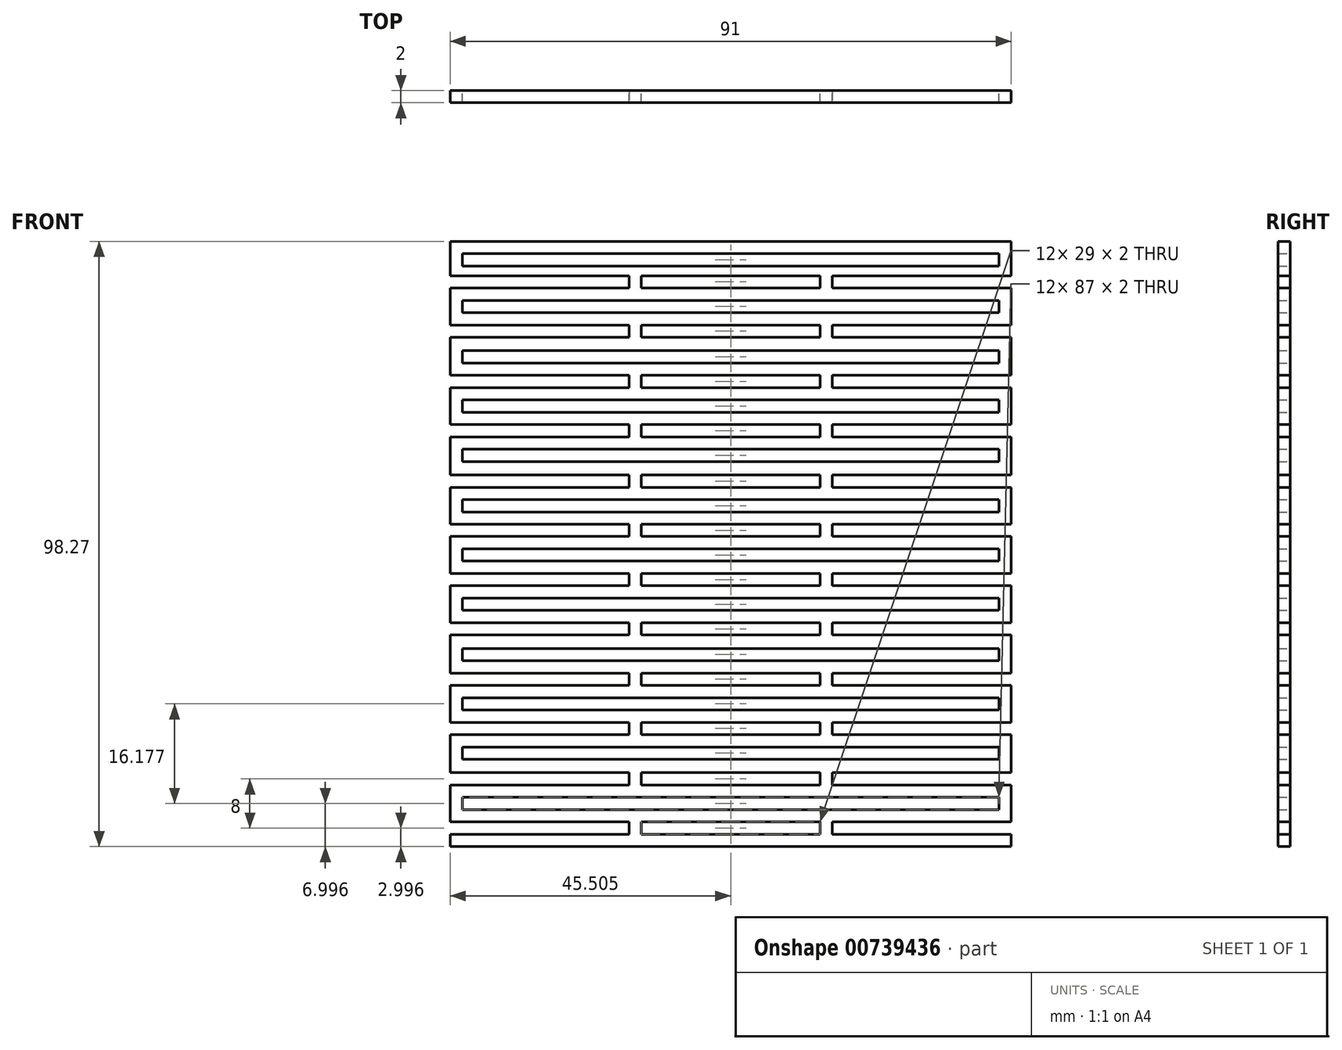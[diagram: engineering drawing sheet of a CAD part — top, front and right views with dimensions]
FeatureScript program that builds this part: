
annotation { "Feature Type Name" : "Feature", "Feature Type Description" : "" }
export const myFeature = defineFeature(function(context is Context, id is Id, definition is map)
    precondition{}
    {
        {
            var Q0;
            Q0=qCreatedBy(makeId("Front.planeOp"),FACE);
            var sketch = newSketch(context, id + "F0", { "sketchPlane" : qUnion([Q0])});
            skLineSegment(sketch, "E0.top", {"start": v(-74.18, -54.88) * mm, "end": v(16.82, -54.88) * mm});
            skLineSegment(sketch, "E0.left", {"start": v(-74.18, 45.12) * mm, "end": v(-74.18, 37.82) * mm});
            skLineSegment(sketch, "E0.right", {"start": v(16.82, 45.12) * mm, "end": v(16.82, 37.82) * mm});
            skLineSegment(sketch, "E1.left", {"start": v(-74.18, -52.88) * mm, "end": v(-74.18, -53.7) * mm});
            skLineSegment(sketch, "E2.bottom", {"start": v(-74.18, -50.88) * mm, "end": v(-45.18, -50.88) * mm});
            skLineSegment(sketch, "E2.top", {"start": v(-74.18, -52.88) * mm, "end": v(-45.18, -52.88) * mm});
            skLineSegment(sketch, "E2.right", {"start": v(-45.18, -50.88) * mm, "end": v(-45.18, -52.88) * mm});
            skLineSegment(sketch, "E3.bottom", {"start": v(16.82, -50.88) * mm, "end": v(-12.18, -50.88) * mm});
            skLineSegment(sketch, "E3.top", {"start": v(16.82, -52.88) * mm, "end": v(-12.18, -52.88) * mm});
            skLineSegment(sketch, "E3.right", {"start": v(-12.18, -50.88) * mm, "end": v(-12.18, -52.88) * mm});
            skPoint(sketch, "E4.oppositeSnap0", {"position": v(2.32, -52.88) * mm});
            skLineSegment(sketch, "E4.bottom", {"start": v(-43.18, -50.88) * mm, "end": v(-14.18, -50.88) * mm});
            skLineSegment(sketch, "E4.top", {"start": v(-43.18, -52.88) * mm, "end": v(-14.18, -52.88) * mm});
            skLineSegment(sketch, "E4.left", {"start": v(-43.18, -50.88) * mm, "end": v(-43.18, -52.88) * mm});
            skLineSegment(sketch, "E4.right", {"start": v(-14.18, -50.88) * mm, "end": v(-14.18, -52.88) * mm});
            skLineSegment(sketch, "E5.bottom", {"start": v(-72.18, -46.88) * mm, "end": v(14.82, -46.88) * mm});
            skLineSegment(sketch, "E5.top", {"start": v(-72.18, -48.88) * mm, "end": v(14.82, -48.88) * mm});
            skLineSegment(sketch, "E5.left", {"start": v(-72.18, -46.88) * mm, "end": v(-72.18, -48.88) * mm});
            skLineSegment(sketch, "E5.right", {"start": v(14.82, -46.88) * mm, "end": v(14.82, -48.88) * mm});
            skLineSegment(sketch, "E6.MirrorCS", {"start": v(-72.18, -40.7) * mm, "end": v(14.82, -40.7) * mm});
            skLineSegment(sketch, "E7.MirrorCS", {"start": v(-72.18, -38.7) * mm, "end": v(14.82, -38.7) * mm});
            skLineSegment(sketch, "E8.MirrorCS", {"start": v(14.82, -40.7) * mm, "end": v(14.82, -38.7) * mm});
            skLineSegment(sketch, "E9.MirrorCS", {"start": v(-72.18, -40.7) * mm, "end": v(-72.18, -38.7) * mm});
            skLineSegment(sketch, "E10.MirrorCS", {"start": v(-74.18, -36.7) * mm, "end": v(-45.18, -36.7) * mm});
            skLineSegment(sketch, "E11.MirrorCS", {"start": v(-74.18, -34.7) * mm, "end": v(-45.18, -34.7) * mm});
            skLineSegment(sketch, "E12.MirrorCS", {"start": v(-43.18, -36.7) * mm, "end": v(-43.18, -34.7) * mm});
            skLineSegment(sketch, "E13.MirrorCS", {"start": v(-45.18, -36.7) * mm, "end": v(-45.18, -34.7) * mm});
            skLineSegment(sketch, "E14.MirrorCS", {"start": v(-43.18, -36.7) * mm, "end": v(-14.18, -36.7) * mm});
            skLineSegment(sketch, "E15.MirrorCS", {"start": v(-43.18, -34.7) * mm, "end": v(-14.18, -34.7) * mm});
            skLineSegment(sketch, "E16.MirrorCS", {"start": v(-14.18, -36.7) * mm, "end": v(-14.18, -34.7) * mm});
            skLineSegment(sketch, "E17.MirrorCS", {"start": v(-12.18, -36.7) * mm, "end": v(-12.18, -34.7) * mm});
            skLineSegment(sketch, "E18.MirrorCS", {"start": v(16.82, -36.7) * mm, "end": v(-12.18, -36.7) * mm});
            skLineSegment(sketch, "E19.MirrorCS", {"start": v(16.82, -34.7) * mm, "end": v(-12.18, -34.7) * mm});
            skLineSegment(sketch, "E20.MirrorCS", {"start": v(-74.18, -44.88) * mm, "end": v(-45.18, -44.88) * mm});
            skLineSegment(sketch, "E21.MirrorCS", {"start": v(-74.18, -42.88) * mm, "end": v(-45.18, -42.88) * mm});
            skLineSegment(sketch, "E22.MirrorCS", {"start": v(-43.18, -44.88) * mm, "end": v(-43.18, -42.88) * mm});
            skLineSegment(sketch, "E23.MirrorCS", {"start": v(-45.18, -44.88) * mm, "end": v(-45.18, -42.88) * mm});
            skLineSegment(sketch, "E24.MirrorCS", {"start": v(-43.18, -44.88) * mm, "end": v(-14.18, -44.88) * mm});
            skLineSegment(sketch, "E25.MirrorCS", {"start": v(-43.18, -42.88) * mm, "end": v(-14.18, -42.88) * mm});
            skLineSegment(sketch, "E26.MirrorCS", {"start": v(-14.18, -44.88) * mm, "end": v(-14.18, -42.88) * mm});
            skLineSegment(sketch, "E27.MirrorCS", {"start": v(-12.18, -44.88) * mm, "end": v(-12.18, -42.88) * mm});
            skLineSegment(sketch, "E28.MirrorCS", {"start": v(16.82, -44.88) * mm, "end": v(-12.18, -44.88) * mm});
            skLineSegment(sketch, "E29.MirrorCS", {"start": v(16.82, -42.88) * mm, "end": v(-12.18, -42.88) * mm});
            skLineSegment(sketch, "E30.MirrorCS", {"start": v(-43.18, -26.7) * mm, "end": v(-43.18, -28.7) * mm});
            skLineSegment(sketch, "E31.MirrorCS", {"start": v(-12.18, -26.7) * mm, "end": v(-12.18, -28.7) * mm});
            skLineSegment(sketch, "E32.MirrorCS", {"start": v(-14.18, -12.53) * mm, "end": v(-14.18, -10.53) * mm});
            skLineSegment(sketch, "E33.MirrorCS", {"start": v(-14.18, -18.53) * mm, "end": v(-14.18, -20.53) * mm});
            skLineSegment(sketch, "E34.MirrorCS", {"start": v(-43.18, -18.53) * mm, "end": v(-43.18, -20.53) * mm});
            skLineSegment(sketch, "E35.MirrorCS", {"start": v(-12.18, -18.53) * mm, "end": v(-12.18, -20.53) * mm});
            skLineSegment(sketch, "E36.MirrorCS", {"start": v(-72.18, -22.7) * mm, "end": v(-72.18, -24.7) * mm});
            skLineSegment(sketch, "E37.MirrorCS", {"start": v(-45.18, -12.53) * mm, "end": v(-45.18, -10.53) * mm});
            skLineSegment(sketch, "E38.MirrorCS", {"start": v(-14.18, -26.7) * mm, "end": v(-14.18, -28.7) * mm});
            skLineSegment(sketch, "E39.MirrorCS", {"start": v(-45.18, -26.7) * mm, "end": v(-45.18, -28.7) * mm});
            skLineSegment(sketch, "E40.MirrorCS", {"start": v(-72.18, -16.53) * mm, "end": v(-72.18, -14.53) * mm});
            skLineSegment(sketch, "E41.MirrorCS", {"start": v(-45.18, -18.53) * mm, "end": v(-45.18, -20.53) * mm});
            skLineSegment(sketch, "E42.MirrorCS", {"start": v(-43.18, -12.53) * mm, "end": v(-43.18, -10.53) * mm});
            skLineSegment(sketch, "E43.MirrorCS", {"start": v(-12.18, -12.53) * mm, "end": v(-12.18, -10.53) * mm});
            skLineSegment(sketch, "E44.MirrorCS", {"start": v(-43.18, -28.7) * mm, "end": v(-14.18, -28.7) * mm});
            skLineSegment(sketch, "E45.MirrorCS", {"start": v(-43.18, -18.53) * mm, "end": v(-14.18, -18.53) * mm});
            skPoint(sketch, "E46.MirrorP", {"position": v(2.32, -10.53) * mm});
            skLineSegment(sketch, "E47.MirrorCS", {"start": v(-43.18, -26.7) * mm, "end": v(-14.18, -26.7) * mm});
            skLineSegment(sketch, "E48.MirrorCS", {"start": v(-43.18, -10.53) * mm, "end": v(-14.18, -10.53) * mm});
            skLineSegment(sketch, "E49.MirrorCS", {"start": v(-43.18, -12.53) * mm, "end": v(-14.18, -12.53) * mm});
            skLineSegment(sketch, "E50.MirrorCS", {"start": v(-43.18, -20.53) * mm, "end": v(-14.18, -20.53) * mm});
            skLineSegment(sketch, "E51.MirrorCS", {"start": v(-72.18, -22.7) * mm, "end": v(14.82, -22.7) * mm});
            skLineSegment(sketch, "E52.MirrorCS", {"start": v(-72.18, -24.7) * mm, "end": v(14.82, -24.7) * mm});
            skLineSegment(sketch, "E53.MirrorCS", {"start": v(-72.18, -16.53) * mm, "end": v(14.82, -16.53) * mm});
            skLineSegment(sketch, "E54.MirrorCS", {"start": v(-72.18, -14.53) * mm, "end": v(14.82, -14.53) * mm});
            skLineSegment(sketch, "E55.MirrorCS", {"start": v(-74.18, -12.53) * mm, "end": v(-45.18, -12.53) * mm});
            skLineSegment(sketch, "E56.MirrorCS", {"start": v(-74.18, -10.53) * mm, "end": v(-45.18, -10.53) * mm});
            skLineSegment(sketch, "E57.MirrorCS", {"start": v(-74.18, -18.53) * mm, "end": v(-45.18, -18.53) * mm});
            skLineSegment(sketch, "E58.MirrorCS", {"start": v(-74.18, -20.53) * mm, "end": v(-45.18, -20.53) * mm});
            skLineSegment(sketch, "E59.MirrorCS", {"start": v(-74.18, -26.7) * mm, "end": v(-45.18, -26.7) * mm});
            skLineSegment(sketch, "E60.MirrorCS", {"start": v(-74.18, -28.7) * mm, "end": v(-45.18, -28.7) * mm});
            skLineSegment(sketch, "E61.MirrorCS", {"start": v(16.82, -28.7) * mm, "end": v(-12.18, -28.7) * mm});
            skLineSegment(sketch, "E62.MirrorCS", {"start": v(16.82, -26.7) * mm, "end": v(-12.18, -26.7) * mm});
            skLineSegment(sketch, "E63.MirrorCS", {"start": v(16.82, -18.53) * mm, "end": v(-12.18, -18.53) * mm});
            skLineSegment(sketch, "E64.MirrorCS", {"start": v(16.82, -20.53) * mm, "end": v(-12.18, -20.53) * mm});
            skLineSegment(sketch, "E65.MirrorCS", {"start": v(16.82, -12.53) * mm, "end": v(-12.18, -12.53) * mm});
            skLineSegment(sketch, "E66.MirrorCS", {"start": v(16.82, -10.53) * mm, "end": v(-12.18, -10.53) * mm});
            skLineSegment(sketch, "E67.MirrorCS", {"start": v(14.82, -16.53) * mm, "end": v(14.82, -14.53) * mm});
            skLineSegment(sketch, "E68.MirrorCS", {"start": v(14.82, -22.7) * mm, "end": v(14.82, -24.7) * mm});
            skPoint(sketch, "E69.oppositeSnap0", {"position": v(13.86, -33.2) * mm});
            skLineSegment(sketch, "E69.bottom", {"start": v(-72.18, -30.7) * mm, "end": v(14.82, -30.7) * mm});
            skLineSegment(sketch, "E69.top", {"start": v(-72.18, -32.7) * mm, "end": v(14.82, -32.7) * mm});
            skLineSegment(sketch, "E69.left", {"start": v(-72.18, -30.7) * mm, "end": v(-72.18, -32.7) * mm});
            skLineSegment(sketch, "E69.right", {"start": v(14.82, -30.7) * mm, "end": v(14.82, -32.7) * mm});
            skPoint(sketch, "E70.MirrorCS.end.orphan", {"position": v(-45.18, -22.7) * mm});
            skPoint(sketch, "E70.MirrorCS.start.orphan", {"position": v(-45.18, -20.53) * mm});
            skPoint(sketch, "E71.orphan", {"position": v(13.86, -31.7) * mm});
            skPoint(sketch, "E72.orphan", {"position": v(13.86, -34.7) * mm});
            skLineSegment(sketch, "E73.bottom", {"start": v(-72.18, -6.53) * mm, "end": v(14.82, -6.53) * mm});
            skLineSegment(sketch, "E73.top", {"start": v(-72.18, -8.53) * mm, "end": v(14.82, -8.53) * mm});
            skLineSegment(sketch, "E73.right", {"start": v(14.82, -6.53) * mm, "end": v(14.82, -8.53) * mm});
            skLineSegment(sketch, "E74.bottom", {"start": v(-74.18, -2.53) * mm, "end": v(-45.18, -2.53) * mm});
            skLineSegment(sketch, "E74.top", {"start": v(-74.18, -4.53) * mm, "end": v(-45.18, -4.53) * mm});
            skLineSegment(sketch, "E74.right", {"start": v(-45.18, -2.53) * mm, "end": v(-45.18, -4.53) * mm});
            skLineSegment(sketch, "E75.bottom", {"start": v(16.82, -2.53) * mm, "end": v(-12.18, -2.53) * mm});
            skLineSegment(sketch, "E75.top", {"start": v(16.82, -4.53) * mm, "end": v(-12.18, -4.53) * mm});
            skLineSegment(sketch, "E75.right", {"start": v(-12.18, -2.53) * mm, "end": v(-12.18, -4.53) * mm});
            skPoint(sketch, "E76.oppositeSnap0", {"position": v(2.32, -4.53) * mm});
            skLineSegment(sketch, "E76.bottom", {"start": v(-43.18, -2.53) * mm, "end": v(-14.18, -2.53) * mm});
            skLineSegment(sketch, "E76.top", {"start": v(-43.18, -4.53) * mm, "end": v(-14.18, -4.53) * mm});
            skLineSegment(sketch, "E76.left", {"start": v(-43.18, -2.53) * mm, "end": v(-43.18, -4.53) * mm});
            skLineSegment(sketch, "E76.right", {"start": v(-14.18, -2.53) * mm, "end": v(-14.18, -4.53) * mm});
            skLineSegment(sketch, "E77.bottom", {"start": v(-72.18, 1.47) * mm, "end": v(14.82, 1.47) * mm});
            skLineSegment(sketch, "E77.top", {"start": v(-72.18, -0.53) * mm, "end": v(14.82, -0.53) * mm});
            skLineSegment(sketch, "E77.left", {"start": v(-72.18, 1.47) * mm, "end": v(-72.18, -0.53) * mm});
            skLineSegment(sketch, "E77.right", {"start": v(14.82, 1.47) * mm, "end": v(14.82, -0.53) * mm});
            skLineSegment(sketch, "E78.MirrorCS", {"start": v(-72.18, 7.65) * mm, "end": v(14.82, 7.65) * mm});
            skLineSegment(sketch, "E79.MirrorCS", {"start": v(-72.18, 9.65) * mm, "end": v(14.82, 9.65) * mm});
            skLineSegment(sketch, "E80.MirrorCS", {"start": v(14.82, 7.65) * mm, "end": v(14.82, 9.65) * mm});
            skLineSegment(sketch, "E81.MirrorCS", {"start": v(-72.18, 7.65) * mm, "end": v(-72.18, 9.65) * mm});
            skLineSegment(sketch, "E82.MirrorCS", {"start": v(-74.18, 11.65) * mm, "end": v(-45.18, 11.65) * mm});
            skLineSegment(sketch, "E83.MirrorCS", {"start": v(-74.18, 13.65) * mm, "end": v(-45.18, 13.65) * mm});
            skLineSegment(sketch, "E84.MirrorCS", {"start": v(-43.18, 11.65) * mm, "end": v(-43.18, 13.65) * mm});
            skLineSegment(sketch, "E85.MirrorCS", {"start": v(-45.18, 11.65) * mm, "end": v(-45.18, 13.65) * mm});
            skLineSegment(sketch, "E86.MirrorCS", {"start": v(-43.18, 11.65) * mm, "end": v(-14.18, 11.65) * mm});
            skLineSegment(sketch, "E87.MirrorCS", {"start": v(-43.18, 13.65) * mm, "end": v(-14.18, 13.65) * mm});
            skLineSegment(sketch, "E88.MirrorCS", {"start": v(-14.18, 11.65) * mm, "end": v(-14.18, 13.65) * mm});
            skLineSegment(sketch, "E89.MirrorCS", {"start": v(-12.18, 11.65) * mm, "end": v(-12.18, 13.65) * mm});
            skLineSegment(sketch, "E90.MirrorCS", {"start": v(16.82, 11.65) * mm, "end": v(-12.18, 11.65) * mm});
            skLineSegment(sketch, "E91.MirrorCS", {"start": v(16.82, 13.65) * mm, "end": v(-12.18, 13.65) * mm});
            skLineSegment(sketch, "E92.MirrorCS", {"start": v(-74.18, 3.47) * mm, "end": v(-45.18, 3.47) * mm});
            skLineSegment(sketch, "E93.MirrorCS", {"start": v(-74.18, 5.47) * mm, "end": v(-45.18, 5.47) * mm});
            skLineSegment(sketch, "E94.MirrorCS", {"start": v(-43.18, 3.47) * mm, "end": v(-43.18, 5.47) * mm});
            skLineSegment(sketch, "E95.MirrorCS", {"start": v(-45.18, 3.47) * mm, "end": v(-45.18, 5.47) * mm});
            skLineSegment(sketch, "E96.MirrorCS", {"start": v(-43.18, 3.47) * mm, "end": v(-14.18, 3.47) * mm});
            skLineSegment(sketch, "E97.MirrorCS", {"start": v(-43.18, 5.47) * mm, "end": v(-14.18, 5.47) * mm});
            skLineSegment(sketch, "E98.MirrorCS", {"start": v(-14.18, 3.47) * mm, "end": v(-14.18, 5.47) * mm});
            skLineSegment(sketch, "E99.MirrorCS", {"start": v(-12.18, 3.47) * mm, "end": v(-12.18, 5.47) * mm});
            skLineSegment(sketch, "E100.MirrorCS", {"start": v(16.82, 3.47) * mm, "end": v(-12.18, 3.47) * mm});
            skLineSegment(sketch, "E101.MirrorCS", {"start": v(16.82, 5.47) * mm, "end": v(-12.18, 5.47) * mm});
            skLineSegment(sketch, "E102.MirrorCS", {"start": v(-43.18, 21.65) * mm, "end": v(-43.18, 19.65) * mm});
            skLineSegment(sketch, "E103.MirrorCS", {"start": v(-12.18, 21.65) * mm, "end": v(-12.18, 19.65) * mm});
            skLineSegment(sketch, "E104.MirrorCS", {"start": v(-14.18, 35.82) * mm, "end": v(-14.18, 37.82) * mm});
            skLineSegment(sketch, "E105.MirrorCS", {"start": v(-14.18, 29.82) * mm, "end": v(-14.18, 27.82) * mm});
            skLineSegment(sketch, "E106.MirrorCS", {"start": v(-43.18, 29.82) * mm, "end": v(-43.18, 27.82) * mm});
            skLineSegment(sketch, "E107.MirrorCS", {"start": v(-12.18, 29.82) * mm, "end": v(-12.18, 27.82) * mm});
            skLineSegment(sketch, "E108.MirrorCS", {"start": v(-72.18, 25.65) * mm, "end": v(-72.18, 23.65) * mm});
            skLineSegment(sketch, "E109.MirrorCS", {"start": v(-45.18, 35.82) * mm, "end": v(-45.18, 37.82) * mm});
            skLineSegment(sketch, "E110.MirrorCS", {"start": v(-14.18, 21.65) * mm, "end": v(-14.18, 19.65) * mm});
            skLineSegment(sketch, "E111.MirrorCS", {"start": v(-45.18, 21.65) * mm, "end": v(-45.18, 19.65) * mm});
            skLineSegment(sketch, "E112.MirrorCS", {"start": v(-72.18, 31.82) * mm, "end": v(-72.18, 33.82) * mm});
            skLineSegment(sketch, "E113.MirrorCS", {"start": v(-45.18, 29.82) * mm, "end": v(-45.18, 27.82) * mm});
            skLineSegment(sketch, "E114.MirrorCS", {"start": v(-43.18, 35.82) * mm, "end": v(-43.18, 37.82) * mm});
            skLineSegment(sketch, "E115.MirrorCS", {"start": v(-12.18, 35.82) * mm, "end": v(-12.18, 37.82) * mm});
            skLineSegment(sketch, "E116.MirrorCS", {"start": v(-43.18, 19.65) * mm, "end": v(-14.18, 19.65) * mm});
            skLineSegment(sketch, "E117.MirrorCS", {"start": v(-43.18, 29.82) * mm, "end": v(-14.18, 29.82) * mm});
            skPoint(sketch, "E118.MirrorP", {"position": v(2.32, 37.82) * mm});
            skLineSegment(sketch, "E119.MirrorCS", {"start": v(-43.18, 21.65) * mm, "end": v(-14.18, 21.65) * mm});
            skLineSegment(sketch, "E120.MirrorCS", {"start": v(-43.18, 37.82) * mm, "end": v(-14.18, 37.82) * mm});
            skLineSegment(sketch, "E121.MirrorCS", {"start": v(-43.18, 35.82) * mm, "end": v(-14.18, 35.82) * mm});
            skLineSegment(sketch, "E122.MirrorCS", {"start": v(-43.18, 27.82) * mm, "end": v(-14.18, 27.82) * mm});
            skLineSegment(sketch, "E123.MirrorCS", {"start": v(-72.18, 25.65) * mm, "end": v(14.82, 25.65) * mm});
            skLineSegment(sketch, "E124.MirrorCS", {"start": v(-72.18, 23.65) * mm, "end": v(14.82, 23.65) * mm});
            skLineSegment(sketch, "E125.MirrorCS", {"start": v(-72.18, 31.82) * mm, "end": v(14.82, 31.82) * mm});
            skLineSegment(sketch, "E126.MirrorCS", {"start": v(-72.18, 33.82) * mm, "end": v(14.82, 33.82) * mm});
            skLineSegment(sketch, "E127.MirrorCS", {"start": v(-74.18, 35.82) * mm, "end": v(-45.18, 35.82) * mm});
            skLineSegment(sketch, "E128.MirrorCS", {"start": v(-74.18, 37.82) * mm, "end": v(-45.18, 37.82) * mm});
            skLineSegment(sketch, "E129.MirrorCS", {"start": v(-74.18, 29.82) * mm, "end": v(-45.18, 29.82) * mm});
            skLineSegment(sketch, "E130.MirrorCS", {"start": v(-74.18, 27.82) * mm, "end": v(-45.18, 27.82) * mm});
            skLineSegment(sketch, "E131.MirrorCS", {"start": v(-74.18, 21.65) * mm, "end": v(-45.18, 21.65) * mm});
            skLineSegment(sketch, "E132.MirrorCS", {"start": v(-74.18, 19.65) * mm, "end": v(-45.18, 19.65) * mm});
            skLineSegment(sketch, "E133.MirrorCS", {"start": v(16.82, 19.65) * mm, "end": v(-12.18, 19.65) * mm});
            skLineSegment(sketch, "E134.MirrorCS", {"start": v(16.82, 21.65) * mm, "end": v(-12.18, 21.65) * mm});
            skLineSegment(sketch, "E135.MirrorCS", {"start": v(16.82, 29.82) * mm, "end": v(-12.18, 29.82) * mm});
            skLineSegment(sketch, "E136.MirrorCS", {"start": v(16.82, 27.82) * mm, "end": v(-12.18, 27.82) * mm});
            skLineSegment(sketch, "E137.MirrorCS", {"start": v(16.82, 35.82) * mm, "end": v(-12.18, 35.82) * mm});
            skLineSegment(sketch, "E138.MirrorCS", {"start": v(16.82, 37.82) * mm, "end": v(-12.18, 37.82) * mm});
            skLineSegment(sketch, "E139.MirrorCS", {"start": v(14.82, 31.82) * mm, "end": v(14.82, 33.82) * mm});
            skLineSegment(sketch, "E140.MirrorCS", {"start": v(14.82, 25.65) * mm, "end": v(14.82, 23.65) * mm});
            skPoint(sketch, "E141.oppositeSnap0", {"position": v(13.86, 15.15) * mm});
            skLineSegment(sketch, "E141.bottom", {"start": v(-72.18, 17.65) * mm, "end": v(14.82, 17.65) * mm});
            skLineSegment(sketch, "E141.top", {"start": v(-72.18, 15.65) * mm, "end": v(14.82, 15.65) * mm});
            skLineSegment(sketch, "E141.left", {"start": v(-72.18, 17.65) * mm, "end": v(-72.18, 15.65) * mm});
            skLineSegment(sketch, "E141.right", {"start": v(14.82, 17.65) * mm, "end": v(14.82, 15.65) * mm});
            skPoint(sketch, "E142.MirrorCS.end.orphan", {"position": v(-45.18, 25.64) * mm});
            skPoint(sketch, "E142.MirrorCS.start.orphan", {"position": v(-45.18, 27.82) * mm});
            skPoint(sketch, "E143.orphan", {"position": v(13.86, 16.65) * mm});
            skPoint(sketch, "E144.orphan", {"position": v(13.86, 13.65) * mm});
            skLineSegment(sketch, "E145.bottom", {"start": v(-72.18, 41.39) * mm, "end": v(14.82, 41.39) * mm});
            skLineSegment(sketch, "E145.top", {"start": v(-72.18, 39.39) * mm, "end": v(14.82, 39.39) * mm});
            skLineSegment(sketch, "E145.left", {"start": v(-72.18, 41.39) * mm, "end": v(-72.18, 39.39) * mm});
            skLineSegment(sketch, "E145.right", {"start": v(14.82, 41.39) * mm, "end": v(14.82, 39.39) * mm});
            skLineSegment(sketch, "E146", {"start": v(-74.18, 43.39) * mm, "end": v(16.82, 43.39) * mm});
            skLineSegment(sketch, "E147.trimOffspring", {"start": v(-74.18, 27.82) * mm, "end": v(-74.18, 21.65) * mm});
            skLineSegment(sketch, "E148.trimOffspring", {"start": v(-74.18, 19.65) * mm, "end": v(-74.18, 13.65) * mm});
            skLineSegment(sketch, "E149.trimOffspring", {"start": v(-74.18, 3.47) * mm, "end": v(-74.18, -2.53) * mm});
            skLineSegment(sketch, "E150.trimOffspring", {"start": v(-74.18, -4.53) * mm, "end": v(-74.18, -10.53) * mm});
            skLineSegment(sketch, "E151.trimOffspring", {"start": v(-74.18, -12.53) * mm, "end": v(-74.18, -18.53) * mm});
            skLineSegment(sketch, "E152.trimOffspring", {"start": v(-74.18, -20.53) * mm, "end": v(-74.18, -26.7) * mm});
            skLineSegment(sketch, "E153.trimOffspring", {"start": v(-74.18, -28.7) * mm, "end": v(-74.18, -34.7) * mm});
            skLineSegment(sketch, "E154.trimOffspring", {"start": v(-74.18, -36.7) * mm, "end": v(-74.18, -42.88) * mm});
            skLineSegment(sketch, "E155.trimOffspring", {"start": v(-74.18, -44.88) * mm, "end": v(-74.18, -50.88) * mm});
            skLineSegment(sketch, "E156.trimOffspring", {"start": v(16.82, -36.7) * mm, "end": v(16.82, -42.88) * mm});
            skLineSegment(sketch, "E157.trimOffspring", {"start": v(16.82, -28.7) * mm, "end": v(16.82, -34.7) * mm});
            skLineSegment(sketch, "E158.trimOffspring", {"start": v(16.82, -20.53) * mm, "end": v(16.82, -26.7) * mm});
            skLineSegment(sketch, "E159.trimOffspring", {"start": v(16.82, -12.53) * mm, "end": v(16.82, -18.53) * mm});
            skLineSegment(sketch, "E160.trimOffspring", {"start": v(16.82, -4.53) * mm, "end": v(16.82, -10.53) * mm});
            skLineSegment(sketch, "E161.trimOffspring", {"start": v(16.82, -44.88) * mm, "end": v(16.82, -50.88) * mm});
            skLineSegment(sketch, "E162.trimOffspring", {"start": v(16.82, -52.88) * mm, "end": v(16.82, -54.88) * mm});
            skLineSegment(sketch, "E163.trimOffspring", {"start": v(16.82, 3.47) * mm, "end": v(16.82, -2.53) * mm});
            skLineSegment(sketch, "E164.trimOffspring", {"start": v(16.82, 11.65) * mm, "end": v(16.82, 5.47) * mm});
            skLineSegment(sketch, "E165.trimOffspring", {"start": v(16.82, 19.65) * mm, "end": v(16.82, 13.65) * mm});
            skLineSegment(sketch, "E166.trimOffspring", {"start": v(-74.18, -52.88) * mm, "end": v(-74.18, -54.88) * mm});
            skLineSegment(sketch, "E167.trimOffspring", {"start": v(-74.18, 11.65) * mm, "end": v(-74.18, 5.47) * mm});
            skLineSegment(sketch, "E168.trimOffspring", {"start": v(16.82, 27.82) * mm, "end": v(16.82, 21.65) * mm});
            skLineSegment(sketch, "E169.trimOffspring", {"start": v(16.82, 35.82) * mm, "end": v(16.82, 29.82) * mm});
            skLineSegment(sketch, "E170.trimOffspring", {"start": v(-74.18, 35.82) * mm, "end": v(-74.18, 29.82) * mm});
            skPoint(sketch, "E171.start.orphan", {"position": v(0, -6.53) * mm});
            skPoint(sketch, "E172.start.orphan", {"position": v(0, -10.53) * mm});
            skLineSegment(sketch, "E173", {"start": v(-72.18, -8.53) * mm, "end": v(-72.18, -6.53) * mm});
            skSolve(sketch);
        }
        {
            var Q0;
            Q0 = qSketchRegion(id + "F0", true);
            extrude(context, id + "F1", {"entities" : qUnion([Q0]), "depth" : 2 * mm, "offsetDistance" : 25 * mm});
        }
    });
